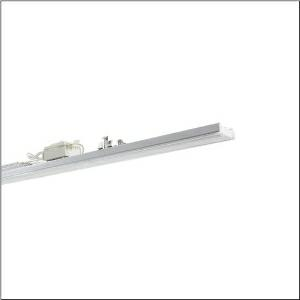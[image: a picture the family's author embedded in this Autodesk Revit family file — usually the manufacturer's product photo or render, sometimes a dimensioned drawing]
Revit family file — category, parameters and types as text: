
# Revit family: licross_r__21_recessed_mo_52tl19de445g_6927
name_source: partatom
category: Lighting Fixtures
units: mm (PartAtom-declared; Revit-internal decimal feet)

## family parameters
Cut with Voids When Loaded = No
Host = Face
Light Source = No
Part Type = Normal
Room Calculation Point = No
Round Connector Dimension = Use Diameter
Shared = No

## types (1)
- --- (1 x LED, 4930 lm, 29.9 W, 4000K)
    Apparent Load = 30 VA
    CIE Flux Codes = 55 90 98 100 100
    Color Rendering = 80
    Color Temperature = 4000K
    Default Elevation = 1800 mm
    Description = Licross® 21 Recessed MO, luminaire insert, of sheet steel, galvanised, coil coated, white, length: 750mm, width: 66mm, height: 67mm, LED rated luminous flux: 4.930lm, light colour: 840, control gear: DALI 2, with plug, 5-pole, with phase selection, mains connection: 220..240V, AC, 50/60Hz, rated input power: 30W, halogen-free wiring, primary light control with lens, of plastic, primary optical cover: cover, of PMMA, light emission: direct distribution, primary light characteristic: double asymmetric, protection rating (complete): IP40, insulation class (complete): insulation class I (protective earthing), certification: CE, ENEC, VDE, UKCA, protection symbol: D if used in an environment without relevant dust loads with corresponding accessories, impact resistance: IK06, permissible ambient temperature for indoor applications: -25..+35°C, corresponds to IFS (International Featured Standards) requirements for safety and quality in the food industry, reducing of maximum allowable ambient temperature of 5°C with ceiling mounting, LABS conformity tested according to VDMA 24364:2018-05, packaging unit: 1 piece
    Height = 58 mm
    Lamp = 1 x LED
    Lamp Light Flux = 4930 lm
    Lamp Power = 29.9 W
    Lamp count = 1
    Length = 750 mm
    Luminous efficacy = 165 lm/W
    Manufacturer = Siteco
    ModVariant = No
    Model = 52TL19DE445G
    Mounting Place = Ceiling
    Mounting Type = Pendant
    Number of Poles = 1
    OnlyDefault = Yes
    Power Factor = 1
    Product Name = Licross® 21 Recessed MO
    Product group = luminaire insert
    ProductGroupID = 902
    Protection Class = Protection class I
    Protection Degree = IP 40
    RLX_Detail_Level = 1
    RLX_Emergency_Light_Flux = 0 lm
    RLX_Emergency_Type = 0
    RLX_Emergency_Type_DB = No
    RlxData = <blob elided: 28741 chars, md5=b27b1aec>
    Socket = socket
    Standby Power = 0 W
    System Light Flux = 4930 lm
    System Power = 30 W
    Type Comments = factory setting: luminous flux: 100 % | dim-lin: 254 | 390 mA
    Type Image = l_1296930.jpg
    URL = http://relux.com
    VarID = @adj_128092
    Voltage = 0 V
    Weight = 0.00 kg
    Width = 66 mm

## geometry (parser evidence)
native form markers: Blend x4, Sweep x9
no freeform markers — native parametric forms only
